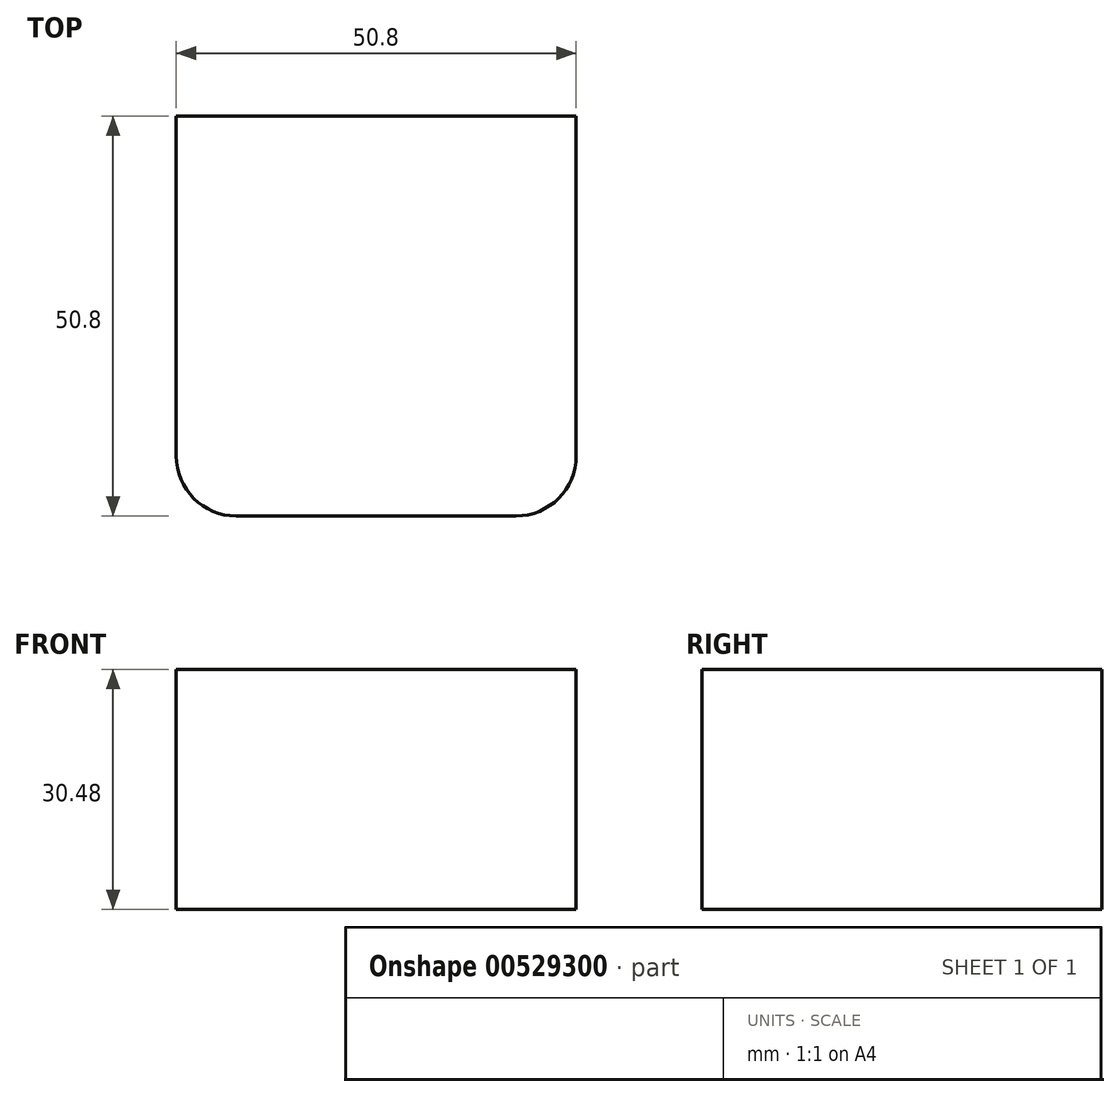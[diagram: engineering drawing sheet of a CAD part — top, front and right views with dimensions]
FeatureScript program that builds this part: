
annotation { "Feature Type Name" : "Feature", "Feature Type Description" : "" }
export const myFeature = defineFeature(function(context is Context, id is Id, definition is map)
    precondition{}
    {
        {
            var Q0;
            Q0=qCreatedBy(makeId("Top.planeOp"),FACE);
            var sketch = newSketch(context, id + "F0", { "sketchPlane" : qUnion([Q0])});
            skLineSegment(sketch, "E0.bottom", {"start": v(0, 0) * mm, "end": v(50.8, 0) * mm});
            skLineSegment(sketch, "E0.top", {"start": v(0, -50.8) * mm, "end": v(50.8, -50.8) * mm});
            skLineSegment(sketch, "E0.left", {"start": v(0, 0) * mm, "end": v(0, -50.8) * mm});
            skLineSegment(sketch, "E0.right", {"start": v(50.8, 0) * mm, "end": v(50.8, -50.8) * mm});
            skSolve(sketch);
        }
        {
            var Q0;
            Q0=makeQuery(id+"F0.imprint","IMPRINT",FACE,{"disambiguationData":[TD([[makeQuery(id+"F0.imprint","IMPRINT",EDGE,{"derivedFrom":sQuery(id+"F0.wireOp",EDGE,"E0.bottom")}),-1.0]])]});
            extrude(context, id + "F1", {"entities" : qUnion([Q0]), "depth" : 30.48 * mm, "offsetDistance" : 25.4 * mm});
        }
        {
            var Q0;
            Q0=makeQuery(id+"F1.opExtrude","SWEPT_EDGE",EDGE,{"disambiguationData":[OSD([sQuery(id+"F0.wireOp",EDGE,"E0.top"),sQuery(id+"F0.wireOp",EDGE,"E0.right")])]});
            var Q1;
            Q1=makeQuery(id+"F1.opExtrude","SWEPT_EDGE",EDGE,{"disambiguationData":[OSD([sQuery(id+"F0.wireOp",EDGE,"E0.top"),sQuery(id+"F0.wireOp",EDGE,"E0.left")])]});
            fillet(context, id + "F2", {"entities" : qUnion([Q0, Q1]), "radius" : 7.62 * mm, "tangentPropagation" : true, "allowEdgeOverflow" : false});
        }
    });
